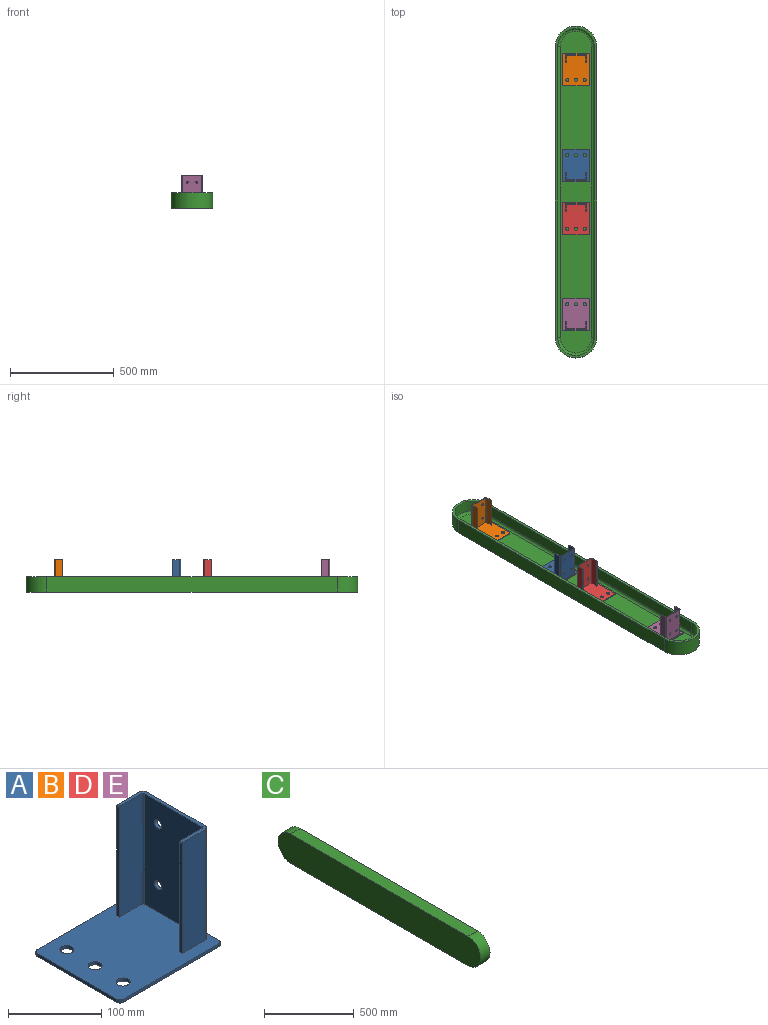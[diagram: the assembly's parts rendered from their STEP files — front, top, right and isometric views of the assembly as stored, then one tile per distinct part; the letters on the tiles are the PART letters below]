
ASSEMBLY  parts=5 mates=4
PART A: 32 faces, bbox 155x130x149 mm
  f0: plane 155x130mm, normal (0,0,1), area 18923.4mm2, adj f1,f2,f3,f4,f6,f7,f8,f9
  f1: plane 120x4mm, normal (-1,0,0), area 480mm2, adj f0,f5,f24,f27
  f2: plane 145x4mm, normal (0,-1,0), area 580mm2, adj f0,f5,f24,f25
  f3: plane 120x4mm, normal (1,0,0), area 480mm2, adj f0,f5,f25,f26
  f4: plane 145x4mm, normal (0,1,0), area 580mm2, adj f0,f5,f26,f27
  f5: plane 155x130mm, normal (0,0,-1), area 19598.4mm2, adj f1,f2,f3,f4,f6,f7,f8,f24
  f6: cylinder r=7.5mm len=15mm, axis (0,0,1), area 188.5mm2, adj f0,f5
  f7: cylinder r=7.5mm len=15mm, axis (0,0,1), area 188.5mm2, adj f0,f5
  f8: cylinder r=7.5mm len=15mm, axis (0,0,1), area 188.5mm2, adj f0,f5
  f9: plane 145x89mm, normal (1,0,0), area 12524.9mm2, adj f0,f17,f18,f19,f28,f29,f30,f31
  f10: plane 145x35mm, normal (0,1,0), area 5074.1mm2, adj f0,f11,f17,f18,f23
  f11: plane 143x4mm, normal (-1,0,0), area 572mm2, adj f0,f10,f12,f23
  f12: plane 145x34mm, normal (0,-1,0), area 4929.1mm2, adj f0,f11,f17,f20,f23
  f13: plane 145x87mm, normal (-1,0,0), area 12234.9mm2, adj f0,f17,f20,f21,f28,f29,f30,f31
  f14: plane 145x34mm, normal (0,1,0), area 4929.1mm2, adj f0,f15,f17,f21,f22
  f15: plane 143x4mm, normal (-1,0,0), area 572mm2, adj f0,f14,f16,f22
  f16: plane 145x35mm, normal (0,-1,0), area 5074.1mm2, adj f0,f15,f17,f19,f22
  f17: plane 99x38mm, normal (0,0,1), area 659mm2, adj f9,f10,f12,f13,f14,f16,f18,f19
  f18: cylinder r=5mm len=145mm, axis (0,0,1), area 1138.8mm2, adj f0,f9,f10,f17
  f19: cylinder r=5mm len=145mm, axis (0,0,-1), area 1138.8mm2, adj f0,f9,f16,f17
  f20: cylinder r=2mm len=145mm, axis (0,0,-1), area 455.5mm2, adj f0,f12,f13,f17
  f21: cylinder r=2mm len=145mm, axis (0,0,1), area 455.5mm2, adj f0,f13,f14,f17
  f22: cylinder r=2mm len=4mm, axis (0,1,0), area 12.6mm2, adj f14,f15,f16,f17
  f23: cylinder r=2mm len=4mm, axis (0,1,0), area 12.6mm2, adj f10,f11,f12,f17
  f24: cylinder r=5mm len=5mm, axis (0,0,1), area 31.4mm2, adj f0,f1,f2,f5
  f25: cylinder r=5mm len=5mm, axis (0,0,-1), area 31.4mm2, adj f0,f2,f3,f5
  f26: cylinder r=5mm len=5mm, axis (0,0,1), area 31.4mm2, adj f0,f3,f4,f5
  f27: cylinder r=5mm len=5mm, axis (0,0,-1), area 31.4mm2, adj f0,f1,f4,f5
  f28: cylinder r=5.5mm len=11mm, axis (1,0,0), area 138.2mm2, adj f9,f13
  f29: cylinder r=5.5mm len=11mm, axis (1,0,0), area 138.2mm2, adj f9,f13
  f30: cylinder r=5.5mm len=11mm, axis (1,0,0), area 138.2mm2, adj f9,f13
  f31: cylinder r=5.5mm len=11mm, axis (1,0,0), area 138.2mm2, adj f9,f13
PART B: same geometry as A
PART C: 15 faces, bbox 75x1600x200 mm
  f0: plane 1400x57mm, normal (0,0,-1), area 79800mm2, adj f4,f8,f10,f13
  f1: plane 1400x75mm, normal (0,0,1), area 105000mm2, adj f2,f4,f11,f12
  f2: plane 1600x200mm, normal (-1,0,0), area 311415.9mm2, adj f1,f3,f11,f12
  f3: plane 1400x75mm, normal (0,0,-1), area 105000mm2, adj f2,f4,f11,f12
  f4: plane 1600x200mm, normal (1,0,0), area 40687.4mm2, adj f0,f1,f3,f5,f10,f11,f12,f13
  f5: plane 1400x57mm, normal (0,0,1), area 79800mm2, adj f4,f6,f10,f13
  f6: cylinder r=12mm len=1400mm, axis (0,1,0), area 26389.4mm2, adj f5,f7,f9,f14
  f7: plane 1552x152mm, normal (1,0,0), area 230945.8mm2, adj f6,f8,f9,f14
  f8: cylinder r=12mm len=1400mm, axis (0,1,0), area 26389.4mm2, adj f0,f7,f9,f14
  f9: torus R=76mm, axis (-1,0,0), area 4952.9mm2, adj f6,f7,f8,f10
  f10: cylinder r=88mm len=176mm, axis (-1,0,0), area 15758.2mm2, adj f0,f4,f5,f9
  f11: cylinder r=100mm len=200mm, axis (-1,0,0), area 23561.9mm2, adj f1,f2,f3,f4
  f12: cylinder r=100mm len=200mm, axis (1,0,0), area 23561.9mm2, adj f1,f2,f3,f4
  f13: cylinder r=88mm len=176mm, axis (1,0,0), area 15758.2mm2, adj f0,f4,f5,f14
  f14: torus R=76mm, axis (1,0,0), area 4952.9mm2, adj f6,f7,f8,f13
PART D: same geometry as A
PART E: same geometry as A
PLACE A rot(axis=(0,0,-1),90deg) t=(-874.21,-477.45,-169.45)mm
PLACE B rot(axis=(0,0,1),90deg) t=(-744.21,-169.45,-169.45)mm
PLACE C rot(axis=(0,-1,0),90deg) t=(-709.21,17.55,-175.45)mm
PLACE D rot(axis=(0,0,1),90deg) t=(-744.21,-887.45,-169.45)mm
PLACE E rot(axis=(0,0,-1),90deg) t=(-874.21,-1195.45,-169.45)mm
MATE fastened E.f0 <-> D.f0  axis (0,0,1) through (-809.21,-1195.45,-165.45)mm
MATE fastened B.f0 <-> A.f0  axis (0,0,1) through (-809.21,-169.45,-165.45)mm
MATE fastened D.f5 <-> C.f7  axis (0,0,-1) through (-809.21,-732.45,-169.45)mm
MATE fastened A.f0 <-> D.f0  axis (0,0,1) through (-809.21,-632.45,-165.45)mm
